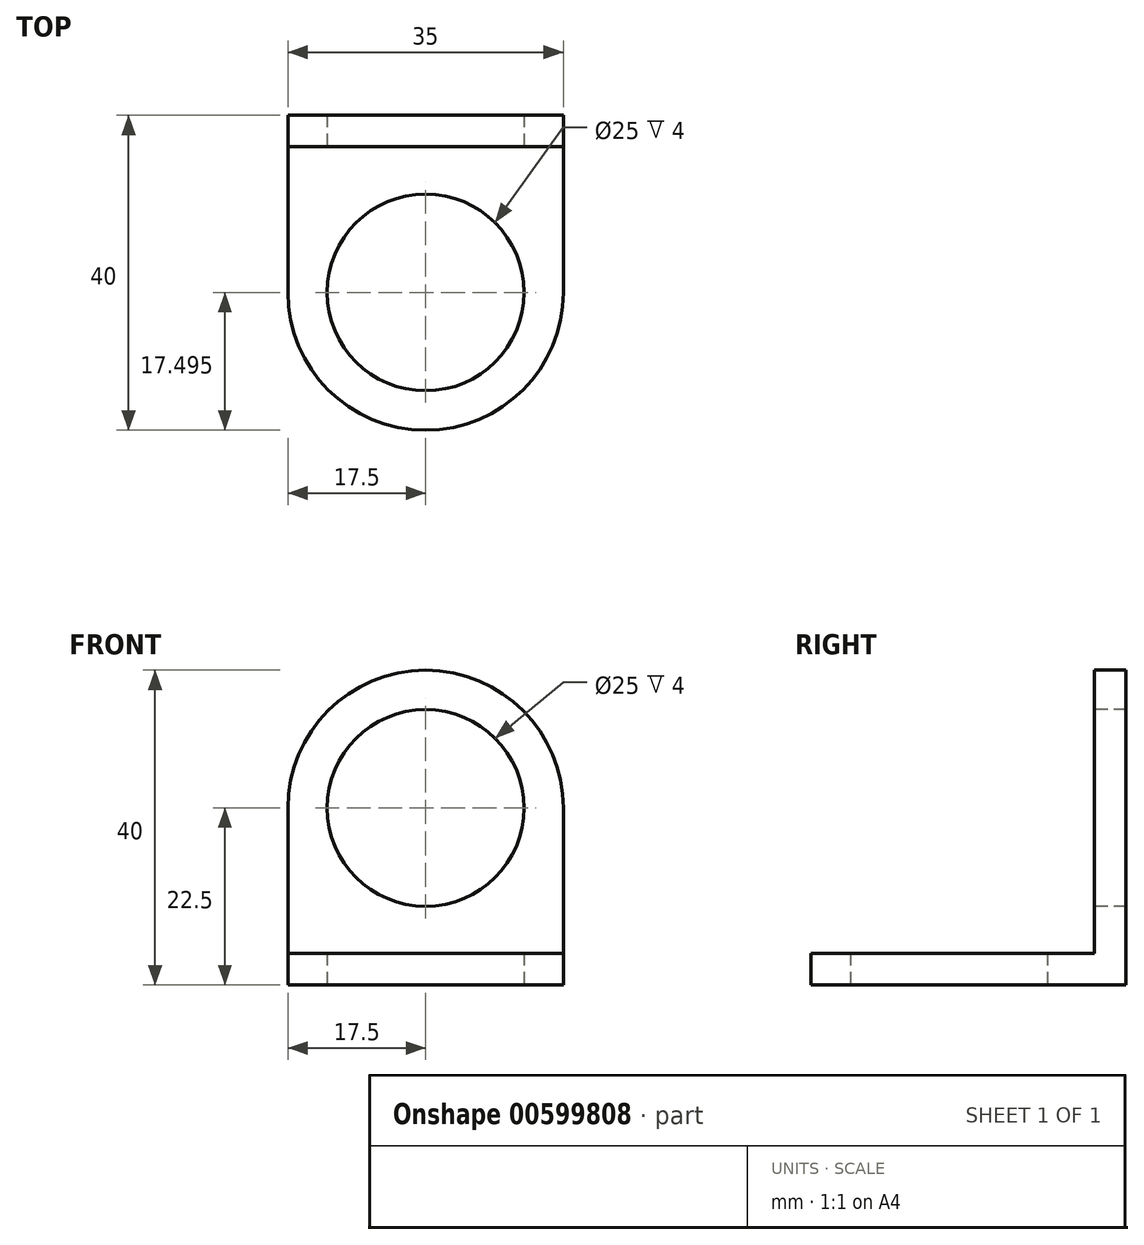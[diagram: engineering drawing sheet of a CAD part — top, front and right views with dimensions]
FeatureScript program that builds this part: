
annotation { "Feature Type Name" : "Feature", "Feature Type Description" : "" }
export const myFeature = defineFeature(function(context is Context, id is Id, definition is map)
    precondition{}
    {
        {
            var Q0;
            Q0=qCreatedBy(makeId("Top.planeOp"),FACE);
            var sketch = newSketch(context, id + "F0", { "sketchPlane" : qUnion([Q0])});
            skLineSegment(sketch, "E0.bottom", {"start": v(-17.5, 0.58) * mm, "end": v(17.5, 0.58) * mm});
            skLineSegment(sketch, "E0.left", {"start": v(-17.5, 0.58) * mm, "end": v(-17.5, -21.92) * mm});
            skLineSegment(sketch, "E0.right", {"start": v(17.5, 0.58) * mm, "end": v(17.5, -21.92) * mm});
            skArc(sketch, "E1", {"start": v(-17.5, -21.92) * mm, "mid": v(0, -39.42) * mm, "end": v(17.5, -21.92) * mm});
            skPoint(sketch, "E2", {"position": v(0, -39.42) * mm});
            skCircle(sketch, "E3", {"center": v(0, -21.92) * mm, "radius": 12.5 * mm});
            skSolve(sketch);
        }
        {
            var Q0;
            Q0 = qSketchRegion(id + "F0", true);
            extrude(context, id + "F1", {"entities" : qUnion([Q0]), "depth" : 4 * mm, "offsetDistance" : 25 * mm});
        }
        {
            var Q0;
            Q0=makeQuery(id+"F1.opExtrude","CAP_FACE",FACE,{"disambiguationData":[OSD([sQuery(id+"F0.wireOp",EDGE,"E0.bottom"),sQuery(id+"F0.wireOp",EDGE,"E0.left"),sQuery(id+"F0.wireOp",EDGE,"E0.right"),sQuery(id+"F0.wireOp",EDGE,"E1"),sQuery(id+"F0.wireOp",EDGE,"E3")])],"isStart":false});
            var sketch = newSketch(context, id + "F2", { "sketchPlane" : qUnion([Q0])});
            skLineSegment(sketch, "E4.bottom", {"start": v(-17.5, 0.58) * mm, "end": v(17.5, 0.58) * mm});
            skLineSegment(sketch, "E4.top", {"start": v(-17.5, -3.42) * mm, "end": v(17.5, -3.42) * mm});
            skLineSegment(sketch, "E4.left", {"start": v(-17.5, 0.58) * mm, "end": v(-17.5, -3.42) * mm});
            skLineSegment(sketch, "E4.right", {"start": v(17.5, 0.58) * mm, "end": v(17.5, -3.42) * mm});
            skSolve(sketch);
        }
        {
            var Q0;
            Q0 = qSketchRegion(id + "F2", true);
            extrude(context, id + "F3", {"entities" : qUnion([Q0]), "operationType" : NewBodyOperationType.ADD, "depth" : 36 * mm, "offsetDistance" : 25 * mm});
        }
        {
            var Q0;
            Q0=makeQuery(id+"F3.opExtrude","SWEPT_FACE",FACE,{"disambiguationData":[OSD([sQuery(id+"F2.wireOp",EDGE,"E4.top")])]});
            var sketch = newSketch(context, id + "F4", { "sketchPlane" : qUnion([Q0])});
            skArc(sketch, "E5", {"start": v(17.5, 22.5) * mm, "mid": v(0, 40) * mm, "end": v(-17.5, 22.5) * mm});
            skCircle(sketch, "E6", {"center": v(0, 22.5) * mm, "radius": 12.5 * mm});
            skPoint(sketch, "E7", {"position": v(0, 40) * mm});
            skLineSegment(sketch, "E8", {"start": v(-17.5, 40) * mm, "end": v(-17.5, 22.5) * mm});
            skLineSegment(sketch, "E9", {"start": v(17.5, 40) * mm, "end": v(17.5, 22.5) * mm});
            skLineSegment(sketch, "E10", {"start": v(17.5, 40) * mm, "end": v(0, 40) * mm});
            skLineSegment(sketch, "E11", {"start": v(0, 40) * mm, "end": v(-17.5, 40) * mm});
            skSolve(sketch);
        }
        {
            var Q0;
            Q0 = qSketchRegion(id + "F4", true);
            extrude(context, id + "F5", {"entities" : qUnion([Q0]), "operationType" : NewBodyOperationType.REMOVE, "oppositeDirection" : true, "depth" : 25 * mm, "offsetDistance" : 25 * mm});
        }
    });
